# Revit family: Wood I Joist-Section
name_source: partatom
category: Detail Items
revit_build: Autodesk Revit Architecture 2012 (Build: 20110210_1515)
units: mm (PartAtom-declared; Revit-internal decimal feet)

## types (21) — shared parameters

## per-type parameters (varying)
| type | Chord Thickness | Chord Width | Depth | Keynote | Web Thickness |
| 1 3/4x9 1/2 | 0' - 1 3/8" | 0' - 1 3/4" | 0' - 9 1/2" | 06 17 00.C1 | 0' - 0 3/8" |
| 1 3/4x11 7/8 | 0' - 1 3/8" | 0' - 1 3/4" | 0' - 11 7/8" | 06 17 00.C2 | 0' - 0 3/8" |
| 1 3/4x14 | 0' - 1 3/8" | 0' - 1 3/4" | 1' - 2" | 06 17 00.C3 | 0' - 0 3/8" |
| 2 1/16x9 1/2 | 0' - 1 3/8" | 0' - 2 1/16" | 0' - 9 1/2" | 06 17 00.C1 | 0' - 0 3/8" |
| 2 1/16x11 7/8 | 0' - 1 3/8" | 0' - 2 1/16" | 0' - 11 7/8" | 06 17 00.C2 | 0' - 0 3/8" |
| 2 1/16x14 | 0' - 1 3/8" | 0' - 2 1/16" | 1' - 2" | 06 17 00.C3 | 0' - 0 3/8" |
| 2 1/16x16 | 0' - 1 3/8" | 0' - 2 1/16" | 1' - 4" | 06 17 00.C4 | 0' - 0 3/8" |
| 2 5/16x9 1/2 | 0' - 1 3/8" | 0' - 2 5/16" | 0' - 9 1/2" | 06 17 00.C1 | 0' - 0 3/8" |
| 2 5/16x11 7/8 | 0' - 1 3/8" | 0' - 2 5/16" | 0' - 11 7/8" | 06 17 00.C2 | 0' - 0 3/8" |
| 2 5/16x14 | 0' - 1 3/8" | 0' - 2 5/16" | 1' - 2" | 06 17 00.C3 | 0' - 0 3/8" |
| 2 5/16x16 | 0' - 1 3/8" | 0' - 2 5/16" | 1' - 4" | 06 17 00.C4 | 0' - 0 3/8" |
| 3 1/2x11 7/8 | 0' - 1 3/4" | 0' - 3 1/2" | 0' - 11 7/8" | 06 17 00.C2 | 0' - 0 7/16" |
| 3 1/2x14 | 0' - 1 3/4" | 0' - 3 1/2" | 1' - 2" | 06 17 00.C3 | 0' - 0 7/16" |
| 3 1/2x16 | 0' - 1 3/4" | 0' - 3 1/2" | 1' - 4" | 06 17 00.C4 | 0' - 0 7/16" |
| 3 1/2x18 | 0' - 1 3/4" | 0' - 3 1/2" | 1' - 6" | 06 17 00.C5 | 0' - 0 1/2" |
| 3 1/2x20 | 0' - 1 3/4" | 0' - 3 1/2" | 1' - 8" | 06 17 00.C6 | 0' - 0 1/2" |
| 3 1/2x22 | 0' - 1 3/4" | 0' - 3 1/2" | 1' - 10" | 06 17 00.C7 | 0' - 0 1/2" |
| 3 1/2x24 | 0' - 1 3/4" | 0' - 3 1/2" | 2' - 0" | 06 17 00.C8 | 0' - 0 1/2" |
| 3 1/2x26 | 0' - 1 3/4" | 0' - 3 1/2" | 2' - 2" | 06 17 00.C9 | 0' - 0 1/2" |
| 3 1/2x28 | 0' - 1 3/4" | 0' - 3 1/2" | 2' - 4" | 06 17 00.C10 | 0' - 0 1/2" |
| 3 1/2x30 | 0' - 1 3/4" | 0' - 3 1/2" | 2' - 6" | 06 17 00.C11 | 0' - 0 1/2" |

## geometry (parser evidence)
native form markers: Sweep x1
no freeform markers — native parametric forms only
